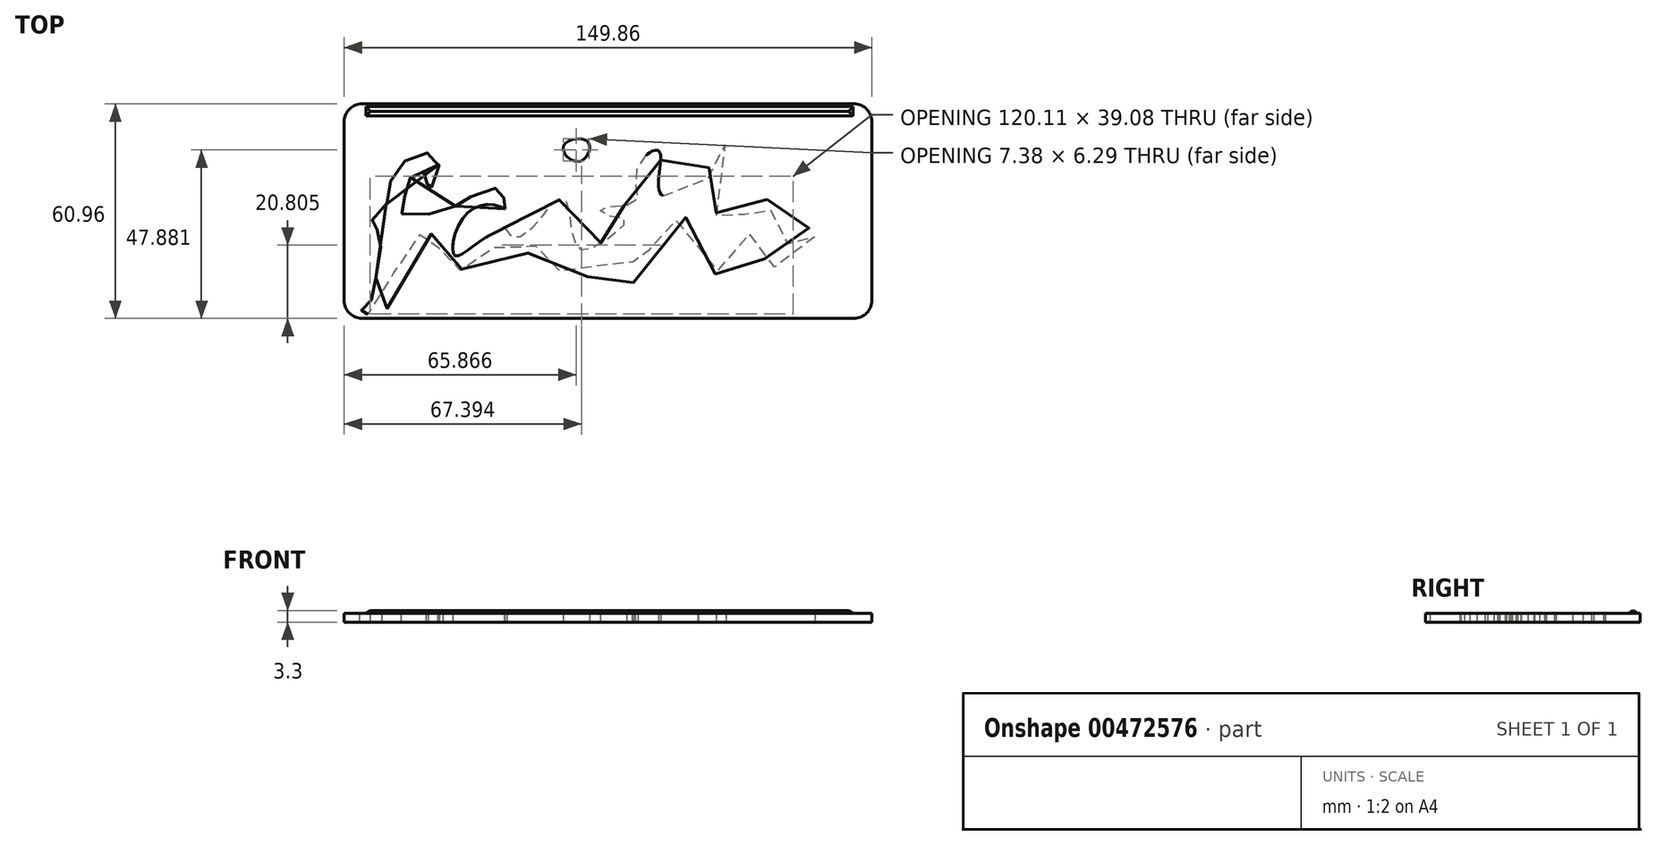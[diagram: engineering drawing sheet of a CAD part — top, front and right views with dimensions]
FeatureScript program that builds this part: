
annotation { "Feature Type Name" : "Feature", "Feature Type Description" : "" }
export const myFeature = defineFeature(function(context is Context, id is Id, definition is map)
    precondition{}
    {
        {
            var Q0;
            Q0=qCreatedBy(makeId("Top.planeOp"),FACE);
            var sketch = newSketch(context, id + "F0", { "sketchPlane" : qUnion([Q0])});
            skLineSegment(sketch, "E0.bottom", {"start": v(69.85, -25.4) * mm, "end": v(-69.85, -25.4) * mm, "construction": true});
            skLineSegment(sketch, "E0.top", {"start": v(69.85, 25.4) * mm, "end": v(-69.85, 25.4) * mm, "construction": true});
            skLineSegment(sketch, "E0.left", {"start": v(69.85, -25.4) * mm, "end": v(69.85, 25.4) * mm, "construction": true});
            skLineSegment(sketch, "E0.right", {"start": v(-69.85, -25.4) * mm, "end": v(-69.85, 25.4) * mm, "construction": true});
            skPoint(sketch, "E0.middle", {"position": v(0, 0) * mm});
            skArc(sketch, "E1", {"start": v(-64.77, 25.4) * mm, "mid": v(-73.44, 29) * mm, "end": v(-69.85, 20.32) * mm});
            skArc(sketch, "E2", {"start": v(69.85, 20.32) * mm, "mid": v(73.44, 29) * mm, "end": v(64.77, 25.4) * mm});
            skArc(sketch, "E3", {"start": v(64.77, -25.4) * mm, "mid": v(73.44, -29) * mm, "end": v(69.85, -20.32) * mm});
            skArc(sketch, "E4", {"start": v(-69.85, -20.32) * mm, "mid": v(-73.44, -29) * mm, "end": v(-64.77, -25.4) * mm});
            skLineSegment(sketch, "E5", {"start": v(-74.93, 25.4) * mm, "end": v(-74.93, -25.4) * mm});
            skLineSegment(sketch, "E6", {"start": v(-69.85, -30.48) * mm, "end": v(69.85, -30.48) * mm});
            skLineSegment(sketch, "E7", {"start": v(74.93, -25.4) * mm, "end": v(74.93, 25.4) * mm});
            skLineSegment(sketch, "E8", {"start": v(69.85, 30.48) * mm, "end": v(-69.85, 30.48) * mm});
            skSolve(sketch);
        }
        {
            var Q0;
            {var subQ0=sQuery(id+"F0.wireOp",EDGE,"E5");Q0=makeQuery(id+"F0.imprint","IMPRINT",FACE,{"disambiguationData":[TD([[makeQuery(id+"F0.imprint","IMPRINT",EDGE,{"derivedFrom":subQ0}),1.0]])]});}
            extrude(context, id + "F1", {"entities" : qUnion([Q0]), "depth" : 2.54 * mm});
        }
        {
            var Q0;
            Q0=makeQuery(id+"F1.opExtrude","CAP_FACE",FACE,{"disambiguationData":[OSD([sQuery(id+"F0.wireOp",EDGE,"E1"),sQuery(id+"F0.wireOp",EDGE,"E2"),sQuery(id+"F0.wireOp",EDGE,"E3"),sQuery(id+"F0.wireOp",EDGE,"E4"),sQuery(id+"F0.wireOp",EDGE,"E5"),sQuery(id+"F0.wireOp",EDGE,"E6"),sQuery(id+"F0.wireOp",EDGE,"E7"),sQuery(id+"F0.wireOp",EDGE,"E8")])],"isStart":false});
            var sketch = newSketch(context, id + "F2", { "sketchPlane" : qUnion([Q0])});
            skPoint(sketch, "E9.firstSnap0", {"position": v(-73.44, 29) * mm});
            skPoint(sketch, "E9.secondSnap0", {"position": v(73.44, -29) * mm});
            skFitSpline(sketch, "E10", {"points": [v(-64.9, -5.87) * mm, v(-67.57, -3.64) * mm, v(-63.36, 1.17) * mm, v(-61.6, 9.08) * mm, v(-54.34, 16.1) * mm, v(-48.53, 15.02) * mm, v(-49.51, 7.54) * mm, v(-51.65, 6.17) * mm, v(-51.03, 9.58) * mm, v(-52.82, 11.2) * mm, v(-56.1, 9.57) * mm, v(-57.73, 4.2) * mm, v(-58.33, -0.99) * mm, v(-44.34, 1.02) * mm, v(-41.15, 2.82) * mm, v(-31.75, 6.44) * mm, v(-30, 4.2) * mm, v(-28.73, 2.97) * mm, v(-29.77, -1.66) * mm, v(-27.75, -7.01) * mm, v(-24.5, -7.04) * mm, v(-17.43, 0) * mm, v(-15.46, 2.66) * mm, v(-12.13, 2.92) * mm, v(-10.62, -3.82) * mm, v(-8.49, -10.36) * mm, v(-5, -10.6) * mm, v(5.3, -2.68) * mm, v(0.4, -1.42) * mm, v(-2.09, 0.71) * mm, v(7.84, 2.57) * mm, v(7.74, 9.61) * mm, v(12.49, 17.01) * mm, v(14.81, 16.3) * mm, v(15.23, 4.62) * mm, v(26.4, 6.5) * mm, v(28.4, 9.46) * mm, v(30.61, 19.7) * mm, v(33.03, 18.97) * mm, v(31.38, 4.58) * mm, v(31.87, -5.83) * mm, v(37.78, -1.94) * mm, v(43.06, 3.4) * mm, v(45.22, 3.25) * mm, v(46.98, -5.42) * mm, v(48.75, -9.13) * mm, v(52.49, -8.53) * mm, v(58.23, -4.38) * mm, v(58.46, -7.8) * mm, v(52.48, -14.43) * mm, v(45.46, -15.1) * mm, v(42.22, -7.42) * mm, v(39.5, -6.62) * mm, v(34.55, -10.97) * mm, v(29.25, -19.46) * mm, v(26.33, -20.06) * mm, v(25.42, 0) * mm, v(22.93, -1.38) * mm, v(12.42, -3.37) * mm, v(12.23, -3.37) * mm, v(9.63, -18.2) * mm, v(7.03, -20.03) * mm, v(7.2, -9.84) * mm, v(3.54, -12.1) * mm, v(-5.26, -18.48) * mm, v(-13.12, -18) * mm, v(-16.51, -8.09) * mm, v(-20.26, -9.91) * mm, v(-27.85, -13.59) * mm, v(-32.77, -10.21) * mm, v(-35.54, -11.04) * mm, v(-41.46, -16.53) * mm, v(-45.7, -17.72) * mm, v(-48.43, -12.6) * mm, v(-46.93, -6.76) * mm, v(-49.13, -6.37) * mm, v(-55.15, -6.71) * mm, v(-58.96, -7.62) * mm, v(-62.06, -26.25) * mm, v(-65.71, -29) * mm, v(-70.6, -29) * mm, v(-69.45, -27.67) * mm, v(-67.16, -25.06) * mm, v(-65.16, -13.36) * mm, v(-64.9, -5.87) * mm]});
            skFitSpline(sketch, "E11", {"points": [v(-11.8, 15.64) * mm, v(-7.12, 14.56) * mm, v(-5.68, 19.68) * mm, v(-12.13, 19.29) * mm, v(-11.8, 15.64) * mm]});
            skSolve(sketch);
        }
        {
            var Q0;
            Q0=makeQuery(id+"F2.imprint","IMPRINT",FACE,{"disambiguationData":[TD([[makeQuery(id+"F2.imprint","IMPRINT",EDGE,{"derivedFrom":sQuery(id+"F2.wireOp",EDGE,"E10")}),-1.0]])]});
            var Q1;
            Q1=makeQuery(id+"F2.imprint","IMPRINT",FACE,{"disambiguationData":[TD([[makeQuery(id+"F2.imprint","IMPRINT",EDGE,{"derivedFrom":sQuery(id+"F2.wireOp",EDGE,"E11")}),1.0]])]});
            var Q2;
            Q2=sQuery(id+"F2.wireOp",EDGE,"E10");
            var Q3;
            Q3=sQuery(id+"F2.wireOp",EDGE,"0bd4d60d-bd50-4eaf-9a3c-2f46c5f9b060");
            var Q4;
            Q4=sQuery(id+"F2.wireOp",EDGE,"E11");
            extrude(context, id + "F3", {"entities" : qUnion([Q0, Q1]), "operationType" : NewBodyOperationType.REMOVE, "surfaceEntities" : qUnion([Q2, Q3, Q4]), "oppositeDirection" : true, "depth" : 25.4 * mm});
        }
        {
            var Q0;
            Q0=makeQuery(id+"F1.opExtrude","CAP_FACE",FACE,{"disambiguationData":[OSD([sQuery(id+"F0.wireOp",EDGE,"E1"),sQuery(id+"F0.wireOp",EDGE,"E2"),sQuery(id+"F0.wireOp",EDGE,"E3"),sQuery(id+"F0.wireOp",EDGE,"E4"),sQuery(id+"F0.wireOp",EDGE,"E5"),sQuery(id+"F0.wireOp",EDGE,"E6"),sQuery(id+"F0.wireOp",EDGE,"E7"),sQuery(id+"F0.wireOp",EDGE,"E8")])],"isStart":false});
            var sketch = newSketch(context, id + "F4", { "sketchPlane" : qUnion([Q0])});
            skFitSpline(sketch, "E12", {"points": [v(-67.58, -25.53) * mm, v(-64.6, -24.88) * mm, v(-59.47, -5.19) * mm, v(-60.87, -1.18) * mm, v(-59, 2.18) * mm, v(-57.7, 9.84) * mm, v(-54.61, 16.46) * mm, v(-50.23, 18.98) * mm, v(-47.34, 15.9) * mm, v(-48.55, 11.42) * mm, v(-49.02, 16.09) * mm, v(-52.65, 16.93) * mm, v(-57.32, 6.66) * mm, v(-57.32, 1.34) * mm, v(-43.88, 0.97) * mm, v(-39.4, 4.33) * mm, v(-33.06, 8.25) * mm, v(-32.97, 8.53) * mm], "startDerivative": vector(68.86, -16.44) * mm, "endDerivative": vector(-2.42, 17.92) * mm});
            skSolve(sketch);
        }
        {
            var Q0;
            Q0=qCreatedBy(makeId("Top.planeOp"),FACE);
            var sketch = newSketch(context, id + "F5", { "sketchPlane" : qUnion([Q0])});
            skLineSegment(sketch, "E13.bottom", {"start": v(232.4, -25.4) * mm, "end": v(92.7, -25.4) * mm, "construction": true});
            skLineSegment(sketch, "E13.top", {"start": v(232.4, 25.4) * mm, "end": v(92.7, 25.4) * mm, "construction": true});
            skLineSegment(sketch, "E13.left", {"start": v(232.4, -25.4) * mm, "end": v(232.4, 25.4) * mm, "construction": true});
            skLineSegment(sketch, "E13.right", {"start": v(92.7, -25.4) * mm, "end": v(92.7, 25.4) * mm, "construction": true});
            skPoint(sketch, "E13.middle", {"position": v(162.56, 0) * mm});
            skArc(sketch, "E14", {"start": v(97.79, 25.4) * mm, "mid": v(89.12, 29) * mm, "end": v(92.7, 20.32) * mm});
            skArc(sketch, "E15", {"start": v(232.4, 20.32) * mm, "mid": v(236, 29) * mm, "end": v(227.33, 25.4) * mm});
            skArc(sketch, "E16", {"start": v(227.33, -25.4) * mm, "mid": v(236, -29) * mm, "end": v(232.4, -20.32) * mm});
            skArc(sketch, "E17", {"start": v(92.7, -20.32) * mm, "mid": v(89.12, -29) * mm, "end": v(97.79, -25.4) * mm});
            skLineSegment(sketch, "E18", {"start": v(87.63, 25.4) * mm, "end": v(87.63, -25.4) * mm});
            skLineSegment(sketch, "E19", {"start": v(92.7, -30.48) * mm, "end": v(232.4, -30.48) * mm});
            skLineSegment(sketch, "E20", {"start": v(237.5, -25.4) * mm, "end": v(237.5, 25.4) * mm});
            skLineSegment(sketch, "E21", {"start": v(232.4, 30.48) * mm, "end": v(92.7, 30.48) * mm});
            skSolve(sketch);
        }
        {
            var Q0;
            {var subQ0=sQuery(id+"F5.wireOp",EDGE,"E18");Q0=makeQuery(id+"F5.imprint","IMPRINT",FACE,{"disambiguationData":[TD([[makeQuery(id+"F5.imprint","IMPRINT",EDGE,{"derivedFrom":subQ0}),1.0]])]});}
            extrude(context, id + "F6", {"entities" : qUnion([Q0]), "depth" : 2.54 * mm});
        }
        {
            var Q0;
            Q0=makeQuery(id+"F6.opExtrude","CAP_FACE",FACE,{"disambiguationData":[OSD([sQuery(id+"F5.wireOp",EDGE,"E14"),sQuery(id+"F5.wireOp",EDGE,"E15"),sQuery(id+"F5.wireOp",EDGE,"E16"),sQuery(id+"F5.wireOp",EDGE,"E17"),sQuery(id+"F5.wireOp",EDGE,"E18"),sQuery(id+"F5.wireOp",EDGE,"E19"),sQuery(id+"F5.wireOp",EDGE,"E20"),sQuery(id+"F5.wireOp",EDGE,"E21")])],"isStart":false});
            var sketch = newSketch(context, id + "F7", { "sketchPlane" : qUnion([Q0])});
            skFitSpline(sketch, "E22", {"points": [v(111.78, 12.75) * mm, v(115.75, 11.51) * mm, v(111.04, 0) * mm, v(117.5, 2.33) * mm, v(123.57, 8.66) * mm, v(124.81, 2.82) * mm, v(133.62, 10.9) * mm, v(135.24, 1.34) * mm, v(139.5, 3.93) * mm, v(142.24, 0) * mm, v(146.96, 0) * mm, v(150.06, 2.82) * mm, v(151.8, 0) * mm, v(159.74, 2.7) * mm, v(162.1, 4.68) * mm, v(163.96, -1.28) * mm, v(173.01, 3.56) * mm, v(177.23, 6.17) * mm, v(176.74, -1.53) * mm, v(182.2, 0) * mm, v(185.18, 1.7) * mm, v(186.42, 0) * mm, v(190.01, 0) * mm, v(194.73, 2.94) * mm, v(196.96, 0) * mm, v(200.81, 2.82) * mm, v(203.54, 0) * mm, v(212.35, 4.93) * mm, v(210.49, -1.53) * mm, v(200.07, -11.33) * mm, v(203.54, -16.17) * mm, v(212.23, -4.75) * mm, v(217.81, -3.01) * mm, v(215.58, 0) * mm, v(216.57, 9.15) * mm, v(209.5, 6.79) * mm, v(206.4, 5.18) * mm, v(208, 9.77) * mm, v(200.81, 6.79) * mm, v(198.08, 5.55) * mm, v(199.45, 9.77) * mm, v(193.49, 10.01) * mm, v(187.16, 6.91) * mm, v(182.45, 4.55) * mm, v(181.7, 8.4) * mm, v(179.22, 11.75) * mm, v(168.3, 4.43) * mm, v(166.31, 8.65) * mm, v(162.84, 10.01) * mm, v(156.76, 6.17) * mm, v(155.27, 10.76) * mm, v(152.04, 8.77) * mm, v(147.45, 5.42) * mm, v(147.58, 11.26) * mm, v(143.98, 9.77) * mm, v(139.76, 8.28) * mm, v(137.03, 5.67) * mm, v(141.87, 15.23) * mm, v(140.25, 19.7) * mm, v(132.44, 13.74) * mm, v(130.2, 18.08) * mm, v(118.54, 9.15) * mm, v(121.64, 16.47) * mm, v(112.7, 16.22) * mm, v(111.78, 12.75) * mm]});
            skSolve(sketch);
        }
        {
            var Q0;
            Q0=makeQuery(id+"F7.imprint","IMPRINT",FACE,{"disambiguationData":[TD([[makeQuery(id+"F7.imprint","IMPRINT",EDGE,{"derivedFrom":sQuery(id+"F7.wireOp",EDGE,"E22")}),1.0]])]});
            extrude(context, id + "F8", {"entities" : qUnion([Q0]), "operationType" : NewBodyOperationType.REMOVE, "oppositeDirection" : true, "depth" : 25.4 * mm, "offsetDistance" : 25.4 * mm});
        }
        {
            var Q0;
            Q0=makeQuery(id+"F4.imprint","IMPRINT",FACE,{"disambiguationData":[TD([[makeQuery(id+"F4.imprint","IMPRINT",EDGE,{"derivedFrom":makeQuery(id+"F1.opExtrude","CAP_EDGE",EDGE,{"disambiguationData":[OSD([sQuery(id+"F0.wireOp",EDGE,"E1")])],"isStart":false})}),1.0]])]});
            var sketch = newSketch(context, id + "F9", { "sketchPlane" : qUnion([Q0])});
            skLineSegment(sketch, "E23.bottom", {"start": v(-68.78, 29.7) * mm, "end": v(69.6, 29.7) * mm});
            skLineSegment(sketch, "E23.top", {"start": v(-68.78, 27.08) * mm, "end": v(69.6, 27.08) * mm});
            skLineSegment(sketch, "E23.left", {"start": v(-68.78, 29.7) * mm, "end": v(-68.78, 27.08) * mm});
            skLineSegment(sketch, "E23.right", {"start": v(69.6, 29.7) * mm, "end": v(69.6, 27.08) * mm});
            skSolve(sketch);
        }
        {
            var Q0;
            Q0 = qSketchRegion(id + "F9", true);
            extrude(context, id + "F10", {"entities" : qUnion([Q0]), "operationType" : NewBodyOperationType.ADD, "depth" : 25.4 * mm, "offsetDistance" : 25.4 * mm, "hasDraft" : true, "draftAngle" : 60 * degree, "draftPullDirection" : true});
        }
        {
            var Q0;
            Q0=makeQuery(id+"F6.opExtrude","SWEPT_BODY",BODY,{"disambiguationData":[OSD([sQuery(id+"F5.wireOp",EDGE,"E14"),sQuery(id+"F5.wireOp",EDGE,"E15"),sQuery(id+"F5.wireOp",EDGE,"E16"),sQuery(id+"F5.wireOp",EDGE,"E17"),sQuery(id+"F5.wireOp",EDGE,"E18"),sQuery(id+"F5.wireOp",EDGE,"E19"),sQuery(id+"F5.wireOp",EDGE,"E20"),sQuery(id+"F5.wireOp",EDGE,"E21")])]});
            deleteBodies(context, id + "F11", {"entities" : qUnion([Q0])});
        }
        {
            var Q0;
            Q0=makeQuery(id+"F4.imprint","IMPRINT",FACE,{"disambiguationData":[TD([[makeQuery(id+"F4.imprint","IMPRINT",EDGE,{"derivedFrom":makeQuery(id+"F1.opExtrude","CAP_EDGE",EDGE,{"disambiguationData":[OSD([sQuery(id+"F0.wireOp",EDGE,"E1")])],"isStart":false})}),1.0]])]});
            var sketch = newSketch(context, id + "F12", { "sketchPlane" : qUnion([Q0])});
            skFitSpline(sketch, "E24", {"points": [v(-28.46, 0) * mm, v(-39.4, 0) * mm, v(-43.61, -12.61) * mm, v(-35.22, -7.72) * mm, v(-28.14, -3.7) * mm, v(-28.46, 0) * mm]});
            skSolve(sketch);
        }
        {
            var Q0;
            Q0 = qSketchRegion(id + "F12", true);
            extrude(context, id + "F13", {"entities" : qUnion([Q0]), "operationType" : NewBodyOperationType.ADD, "oppositeDirection" : true, "depth" : 2.54 * mm, "offsetDistance" : 25.4 * mm});
        }
    });
